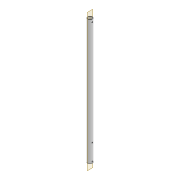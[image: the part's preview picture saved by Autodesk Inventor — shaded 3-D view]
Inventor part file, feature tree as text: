
AUTODESK INVENTOR PART (.ipt)
format: ipt  version: 2022 (Build 260153000, 153)  size: 105,984 bytes
history: native  units: mm
features: extrude x2, sketch x2
ambient origin geometry x8: Origin, YZ Plane, XZ Plane, XY Plane, X Axis, Y Axis, Z Axis, Center Point
bodies: Solid1 (feature_tree)
feature tree (4):
  extrude  "Extrusion1"  Depth=10.0mm
  extrude  "Extrusion2"  Depth=46.0mm
  sketch  "Sketch1"  dims[d0=12.0mm d1=10.0mm]
  sketch  "Sketch2"  dims[d2=320.0mm d3=0.0mm d4=3.0mm d5=3.0mm d6=4.0mm d7=46.0mm d8=320.0mm d9=0.0mm d10=3.0mm d11=6.5mm]
